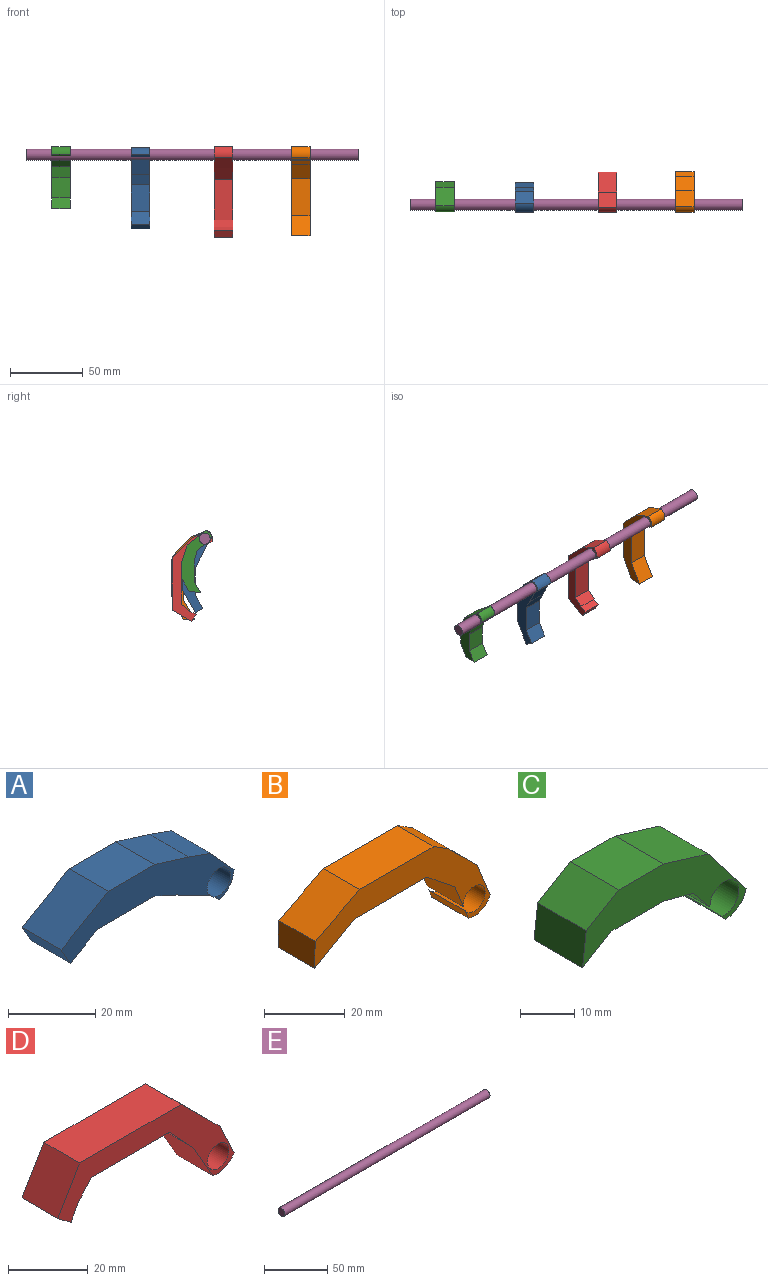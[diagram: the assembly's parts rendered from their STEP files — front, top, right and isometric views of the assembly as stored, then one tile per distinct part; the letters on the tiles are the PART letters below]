
ASSEMBLY  parts=5 mates=4
PART A: 15 faces, bbox 56x12.7x20.3 mm
  f0: plane 12.7x1.64mm, normal (-0.7,0,-0.72), area 29mm2, adj f1,f2,f13,f14
  f1: plane 55.97x20.33mm, normal (0,-1,0), area 439.4mm2, adj f0,f3,f4,f5,f6,f7,f8,f9
  f2: plane 55.97x20.33mm, normal (0,1,0), area 439.4mm2, adj f0,f3,f4,f5,f6,f7,f8,f9
  f3: plane 12.7x10.72mm, normal (-0.46,0,-0.89), area 153mm2, adj f1,f2,f4,f13
  f4: plane 12.7x6.91mm, normal (-0.42,0,-0.91), area 96.5mm2, adj f1,f2,f3,f12
  f5: plane 12.7x8.26mm, normal (0.74,0,0.67), area 141.6mm2, adj f1,f2,f6,f14
  f6: plane 12.7x7.2mm, normal (0.34,0,0.94), area 97.1mm2, adj f1,f2,f5,f7
  f7: plane 12.7x10.94mm, normal (0.3,0,0.96), area 145.4mm2, adj f1,f2,f6,f8
  f8: plane 15.12x12.7mm, normal (0,0,1), area 192mm2, adj f1,f2,f7,f9
  f9: plane 15.23x12.7mm, normal (-0.5,0,0.86), area 223.7mm2, adj f1,f2,f8,f10
  f10: plane 12.7x5.18mm, normal (-0.86,0,-0.5), area 76.1mm2, adj f1,f2,f9,f11
  f11: plane 12.7x8.92mm, normal (0.5,0,-0.86), area 131mm2, adj f1,f2,f10,f12
  f12: plane 18.42x12.7mm, normal (0,0,-1), area 233.9mm2, adj f1,f2,f4,f11
  f13: cylinder r=3.8mm len=12.7mm, axis (0,-1,0), area 278mm2, adj f0,f1,f2,f3
  f14: cylinder r=6.5mm len=12.7mm, axis (0,-1,0), area 106.1mm2, adj f0,f1,f2,f5
PART B: 15 faces, bbox 61.3x12.7x28 mm
  f0: plane 61.33x28mm, normal (0,-1,0), area 508.8mm2, adj f2,f3,f4,f5,f6,f7,f8,f9
  f1: plane 61.33x28mm, normal (0,1,0), area 508.8mm2, adj f2,f3,f4,f5,f6,f7,f8,f9
  f2: plane 12.7x7.42mm, normal (-0.93,0,-0.36), area 101.2mm2, adj f0,f1,f12,f13
  f3: plane 12.7x2.65mm, normal (-0.93,0,-0.36), area 36.2mm2, adj f0,f1,f13,f14
  f4: plane 12.7x11.13mm, normal (0.93,0,0.37), area 152.2mm2, adj f0,f1,f5,f14
  f5: plane 12.7x9.95mm, normal (0.71,0,0.71), area 178.8mm2, adj f0,f1,f4,f6
  f6: plane 12.7x5.15mm, normal (0.54,0,0.84), area 77.5mm2, adj f0,f1,f5,f7
  f7: plane 25.99x12.7mm, normal (0,0,1), area 330.1mm2, adj f0,f1,f6,f8
  f8: plane 15.49x12.7mm, normal (-0.46,0,0.89), area 221.2mm2, adj f0,f1,f7,f9
  f9: plane 12.7x7.98mm, normal (-1,0,0.04), area 101.4mm2, adj f0,f1,f8,f10
  f10: plane 13.86x12.7mm, normal (0.5,0,-0.87), area 203.1mm2, adj f0,f1,f9,f11
  f11: plane 25.46x12.7mm, normal (0,0,-1), area 323.4mm2, adj f0,f1,f10,f12
  f12: plane 12.7x9.83mm, normal (-0.63,0,-0.78), area 160.8mm2, adj f0,f1,f2,f11
  f13: cylinder r=3.8mm len=12.7mm, axis (0,-1,0), area 282.2mm2, adj f0,f1,f2,f3
  f14: cylinder r=5.83mm len=12.7mm, axis (0,-1,0), area 117.2mm2, adj f0,f1,f3,f4
PART C: 14 faces, bbox 42.8x12.7x20.6 mm
  f0: plane 42.8x20.59mm, normal (0,-1,0), area 313.8mm2, adj f2,f3,f4,f5,f6,f7,f8,f9
  f1: plane 42.8x20.59mm, normal (0,1,0), area 313.8mm2, adj f2,f3,f4,f5,f6,f7,f8,f9
  f2: plane 12.7x5.25mm, normal (-0.77,0,-0.64), area 86.8mm2, adj f0,f1,f5,f12
  f3: plane 12.7x1.17mm, normal (-0.77,0,-0.64), area 19.3mm2, adj f0,f1,f12,f13
  f4: plane 13.77x12.7mm, normal (0,0,-1), area 174.8mm2, adj f0,f1,f5,f11
  f5: plane 12.7x7.77mm, normal (-0.26,0,-0.97), area 102.3mm2, adj f0,f1,f2,f4
  f6: plane 12.71x12.7mm, normal (0.79,0,0.62), area 204.8mm2, adj f0,f1,f7,f13
  f7: plane 12.7x11.66mm, normal (0.29,0,0.96), area 154.9mm2, adj f0,f1,f6,f8
  f8: plane 12.7x11.66mm, normal (0,0,1), area 148.1mm2, adj f0,f1,f7,f9
  f9: plane 12.7x8.58mm, normal (-0.5,0,0.86), area 126.3mm2, adj f0,f1,f8,f10
  f10: plane 12.7x7.94mm, normal (-0.99,0,0.12), area 101.5mm2, adj f0,f1,f9,f11
  f11: plane 12.7x7.45mm, normal (0.52,0,-0.85), area 110.8mm2, adj f0,f1,f4,f10
  f12: cylinder r=3.8mm len=12.7mm, axis (0,-1,0), area 238.1mm2, adj f0,f1,f2,f3
  f13: cylinder r=5.26mm len=12.7mm, axis (0,-1,0), area 96.2mm2, adj f0,f1,f3,f6
PART D: 14 faces, bbox 62.6x12.7x27.7 mm
  f0: plane 12.7x10.6mm, normal (0.91,0,0.42), area 148.5mm2, adj f1,f2,f11,f13
  f1: plane 62.61x27.75mm, normal (0,-1,0), area 490.2mm2, adj f0,f3,f4,f5,f6,f7,f8,f9
  f2: plane 62.61x27.75mm, normal (0,1,0), area 490.2mm2, adj f0,f3,f4,f5,f6,f7,f8,f9
  f3: plane 36.1x12.7mm, normal (0,0,1), area 458.4mm2, adj f1,f2,f4,f11
  f4: plane 13.22x12.7mm, normal (-0.86,0,0.51), area 194.6mm2, adj f1,f2,f3,f5
  f5: plane 12.7x4.77mm, normal (-0.6,0,-0.8), area 75.4mm2, adj f1,f2,f4,f6
  f6: plane 12.7x4.67mm, normal (0.89,0,-0.45), area 66.4mm2, adj f1,f2,f5,f7
  f7: plane 12.7x5.56mm, normal (0.75,0,-0.66), area 93.6mm2, adj f1,f2,f6,f8
  f8: plane 27.88x12.7mm, normal (0,0,-1), area 354.1mm2, adj f1,f2,f7,f9
  f9: plane 12.7x8.78mm, normal (-0.73,0,-0.68), area 152.8mm2, adj f1,f2,f8,f10
  f10: plane 12.7x12.2mm, normal (-0.87,0,-0.5), area 178.8mm2, adj f1,f2,f9,f13
  f11: plane 13.82x13.75mm, normal (0.71,0,0.71), area 247.5mm2, adj f0,f1,f2,f3
  f12: cylinder r=3.8mm len=12.7mm, axis (0,-1,0), area 303mm2, adj f1,f2
  f13: cylinder r=6.64mm len=12.7mm, axis (0,-1,0), area 112.1mm2, adj f0,f1,f2,f10
PART E: 3 faces, bbox 228.6x7.6x7.6 mm
  f0: cylinder r=3.78mm len=228.6mm, axis (-1,0,0), area 5436mm2, adj f1,f2
  f1: plane 7.57x7.57mm, normal (1,0,0), area 45mm2, adj f0
  f2: plane 7.57x7.57mm, normal (-1,0,0), area 45mm2, adj f0
PLACE A rot(axis=(-0.58,-0.58,-0.58),120deg) t=(85.09,6.43,-20.7)mm
PLACE B rot(axis=(-0.58,-0.58,-0.58),120deg) t=(195.58,14.81,-18.25)mm
PLACE C rot(axis=(-0.58,-0.58,-0.58),120deg) t=(30.48,7.27,-15.95)mm
PLACE D rot(axis=(-0.58,-0.58,-0.58),120deg) t=(142.24,15.95,-20.7)mm
PLACE E at identity
MATE revolute B.f13 <-> E.f0  axis (-1,0,0) through (182.88,0,0)mm
MATE revolute D.f12 <-> E.f0  axis (-1,0,0) through (129.54,0,0)mm
MATE revolute C.f12 <-> E.f0  axis (-1,0,0) through (17.78,0,0)mm
MATE revolute A.f13 <-> E.f0  axis (-1,0,0) through (72.39,0,0)mm
